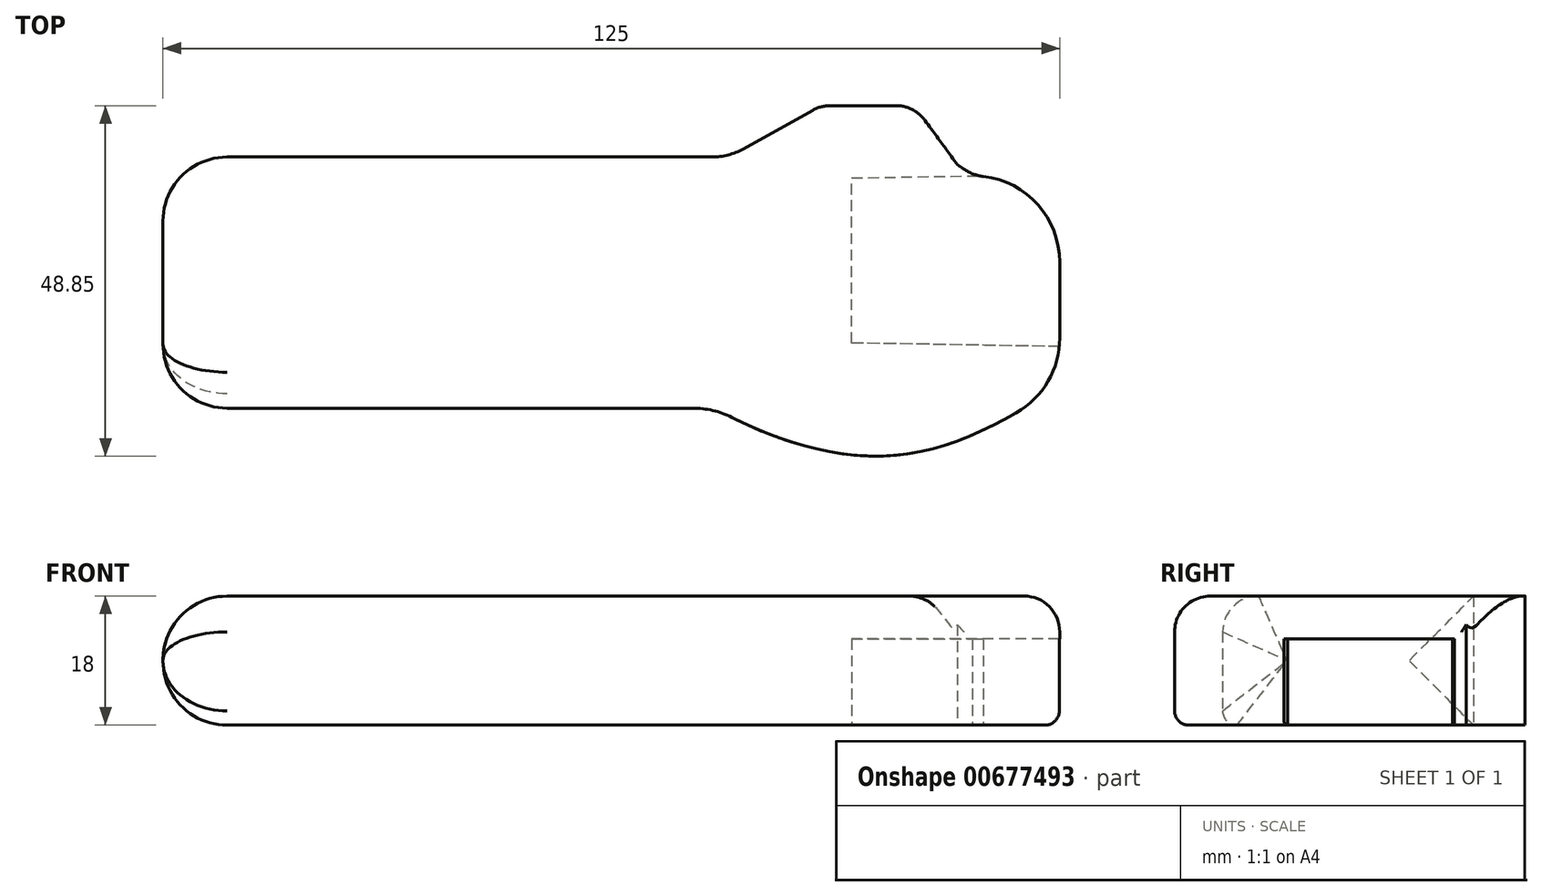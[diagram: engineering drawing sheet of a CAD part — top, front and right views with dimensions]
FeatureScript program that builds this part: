
annotation { "Feature Type Name" : "Feature", "Feature Type Description" : "" }
export const myFeature = defineFeature(function(context is Context, id is Id, definition is map)
    precondition{}
    {
        {
            var Q0;
            Q0=qCreatedBy(makeId("Top.planeOp"),FACE);
            var sketch = newSketch(context, id + "F0", { "sketchPlane" : qUnion([Q0])});
            skLineSegment(sketch, "E0", {"start": v(0, 0) * mm, "end": v(0, 23) * mm});
            skLineSegment(sketch, "E1", {"start": v(0, 23) * mm, "end": v(16.79, 23.29) * mm});
            skLineSegment(sketch, "E2", {"start": v(29, 11.3) * mm, "end": v(29, -0.5) * mm});
            skLineSegment(sketch, "E3", {"start": v(29, -0.5) * mm, "end": v(0, 0) * mm});
            skLineSegment(sketch, "E4.bottom", {"start": v(-19.49, 25.92) * mm, "end": v(-96, 25.92) * mm});
            skLineSegment(sketch, "E4.top", {"start": v(-22.13, -9.08) * mm, "end": v(-96, -9.08) * mm});
            skLineSegment(sketch, "E4.left", {"start": v(29, 29) * mm, "end": v(29, 0.7) * mm});
            skLineSegment(sketch, "E4.right", {"start": v(-96, 25.92) * mm, "end": v(-96, -9.08) * mm});
            skPoint(sketch, "E5", {"position": v(17, 23.3) * mm});
            skPoint(sketch, "E6.visualSharp", {"position": v(29, 23.5) * mm});
            skArc(sketch, "E6.filletArc", {"start": v(29, 11.3) * mm, "mid": v(25.95, 19.28) * mm, "end": v(18.35, 23.21) * mm});
            skLineSegment(sketch, "E7", {"start": v(15.63, 24.23) * mm, "end": v(14.72, 24.86) * mm});
            skPoint(sketch, "E8.newPointA", {"position": v(29, 25.92) * mm});
            skArc(sketch, "E9.filletArc", {"start": v(15.63, 24.23) * mm, "mid": v(16.93, 23.56) * mm, "end": v(18.35, 23.21) * mm});
            skFitSpline(sketch, "E10", {"points": [v(29, -6) * mm, v(6.83, -15.59) * mm, v(-19.16, -9.08) * mm], "startDerivative": vector(-44.85, -29.12) * mm, "endDerivative": vector(-51.39, 28.46) * mm});
            skArc(sketch, "E11.filletArc", {"start": v(-16.74, -10.36) * mm, "mid": v(-19.36, -9.4) * mm, "end": v(-22.13, -9.08) * mm});
            skArc(sketch, "E12.filletArc", {"start": v(22.94, -9.72) * mm, "mid": v(27.37, -5.33) * mm, "end": v(29, 0.7) * mm});
            skLineSegment(sketch, "E13", {"start": v(16.79, 23.29) * mm, "end": v(18.35, 23.21) * mm});
            skLineSegment(sketch, "E14", {"start": v(-15.11, 27.05) * mm, "end": v(-5.4, 32.45) * mm});
            skLineSegment(sketch, "E15", {"start": v(-2.98, 33.08) * mm, "end": v(6.18, 33.08) * mm});
            skLineSegment(sketch, "E16", {"start": v(10.21, 31.03) * mm, "end": v(14.72, 24.86) * mm});
            skPoint(sketch, "E17.visualSharp", {"position": v(-4.27, 33.08) * mm});
            skArc(sketch, "E17.filletArc", {"start": v(-2.98, 33.08) * mm, "mid": v(-4.23, 32.92) * mm, "end": v(-5.4, 32.45) * mm});
            skPoint(sketch, "E18.visualSharp", {"position": v(8.72, 33.08) * mm});
            skArc(sketch, "E18.filletArc", {"start": v(10.21, 31.03) * mm, "mid": v(8.44, 32.54) * mm, "end": v(6.18, 33.08) * mm});
            skArc(sketch, "E19.filletArc", {"start": v(-19.49, 25.92) * mm, "mid": v(-17.23, 26.2) * mm, "end": v(-15.11, 27.05) * mm});
            skSolve(sketch);
        }
        {
            var Q0;
            {var subQ1=sQuery(id+"F0.wireOp",EDGE,"E0");Q0=makeQuery(id+"F0.imprint","IMPRINT",FACE,{"disambiguationData":[TD([[makeQuery(id+"F0.imprint","IMPRINT",EDGE,{"derivedFrom":subQ1}),1.0]])]});}
            var Q1;
            {var subQ5=sQuery(id+"F0.wireOp",EDGE,"E0");Q1=makeQuery(id+"F0.imprint","IMPRINT",FACE,{"disambiguationData":[TD([[makeQuery(id+"F0.imprint","IMPRINT",EDGE,{"derivedFrom":subQ5}),-1.0]])]});}
            extrude(context, id + "F1", {"entities" : qUnion([Q0, Q1]), "depth" : 18 * mm, "offsetDistance" : 25 * mm});
        }
        {
            var Q0;
            {var subQ5=sQuery(id+"F0.wireOp",EDGE,"E0");Q0=makeQuery(id+"F0.imprint","IMPRINT",FACE,{"disambiguationData":[TD([[makeQuery(id+"F0.imprint","IMPRINT",EDGE,{"derivedFrom":subQ5}),-1.0]])]});}
            extrude(context, id + "F2", {"entities" : qUnion([Q0]), "operationType" : NewBodyOperationType.REMOVE, "oppositeDirection" : true, "depth" : -12 * mm, "offsetDistance" : 25 * mm});
        }
        {
            var Q0;
            Q0=makeQuery(id+"F1.opExtrude","CAP_EDGE",EDGE,{"disambiguationData":[OSD([sQuery(id+"F0.wireOp",EDGE,"E4.right")])],"isStart":false});
            var Q1;
            Q1=makeQuery(id+"F1.opExtrude","SWEPT_EDGE",EDGE,{"disambiguationData":[OSD([sQuery(id+"F0.wireOp",EDGE,"E4.bottom"),sQuery(id+"F0.wireOp",EDGE,"E4.right")])]});
            var Q2;
            Q2=makeQuery(id+"F1.opExtrude","CAP_EDGE",EDGE,{"disambiguationData":[OSD([sQuery(id+"F0.wireOp",EDGE,"E4.right")])],"isStart":true});
            var Q3;
            Q3=makeQuery(id+"F1.opExtrude","SWEPT_EDGE",EDGE,{"disambiguationData":[OSD([sQuery(id+"F0.wireOp",EDGE,"E4.top"),sQuery(id+"F0.wireOp",EDGE,"E4.right")])]});
            fillet(context, id + "F3", {"entities" : qUnion([Q0, Q1, Q2, Q3]), "radius" : 8.93 * mm, "tangentPropagation" : true, "allowEdgeOverflow" : false});
        }
        {
            var Q0;
            Q0=makeQuery(id+"F1.opExtrude","CAP_EDGE",EDGE,{"disambiguationData":[OSD([sQuery(id+"F0.wireOp",EDGE,"E4.top")])],"isStart":false});
            fillet(context, id + "F4", {"entities" : qUnion([Q0]), "radius" : 5 * mm, "tangentPropagation" : true, "allowEdgeOverflow" : false});
        }
        {
            var Q0;
            Q0=makeQuery(id+"F1.opExtrude","CAP_EDGE",EDGE,{"disambiguationData":[OSD([sQuery(id+"F0.wireOp",EDGE,"E4.top")])],"isStart":true});
            fillet(context, id + "F5", {"entities" : qUnion([Q0]), "radius" : 2 * mm, "tangentPropagation" : true, "allowEdgeOverflow" : false});
        }
    });
